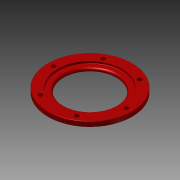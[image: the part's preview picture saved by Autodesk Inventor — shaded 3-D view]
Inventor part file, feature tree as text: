
AUTODESK INVENTOR PART (.ipt)
format: ipt  version: 2015 (Build 190159000, 159)  size: 164,352 bytes
history: native  units: mm
features: sketch x2, revolve x1, hole x1, fillet x1, projected_geometry x1
ambient origin geometry x8: Origin, YZ Plane, XZ Plane, XY Plane, X Axis, Y Axis, Z Axis, Center Point
bodies: Volumenkörper1 (feature_tree)
feature tree (6):
  revolve  "Umdrehung1"
  hole  "Bohrung1"  [1 undecoded]
  fillet  "Rundung1"  Radius=7.0mm
  sketch  "Skizze1"  dims[d0=15.0mm d1=45.0mm d2=7.0mm]
  sketch  "Skizze2"  dims[d3=37.0mm d6=90.0deg d7=37.0mm d8=59.0mm d9=51.0mm d10=60.0mm d12=360.0deg d14=45.0mm d15=3.0mm d16=6.0mm d17=4.0mm d18=2.0mm d19=90.0deg d20=8.0mm d21=20.594885mm d22=0.25mm d23=1.5mm d24=2.0mm d25=1.45mm]
  projected_geometry  "Projizierte Kontur1"
note: 1 required parameter value undecoded (feature->parameter linkage not recoverable at this tier; creation-order binding heuristic only, values carry confidence <= 0.55)
